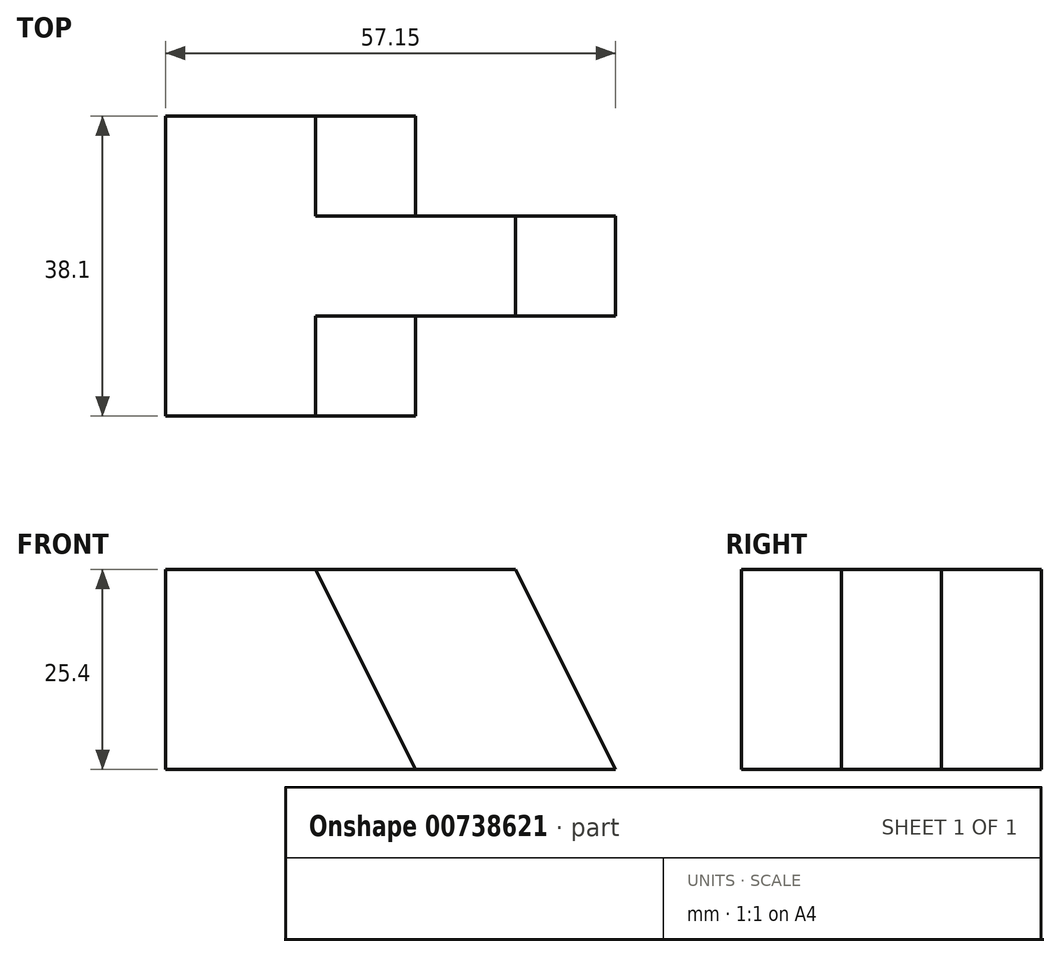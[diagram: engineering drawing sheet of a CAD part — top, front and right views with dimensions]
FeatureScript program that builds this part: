
annotation { "Feature Type Name" : "Feature", "Feature Type Description" : "" }
export const myFeature = defineFeature(function(context is Context, id is Id, definition is map)
    precondition{}
    {
        {
            var Q0;
            Q0=qCreatedBy(makeId("Front.planeOp"),FACE);
            var sketch = newSketch(context, id + "F0", { "sketchPlane" : qUnion([Q0])});
            skLineSegment(sketch, "E0.bottom", {"start": v(0, 0) * mm, "end": v(57.15, 0) * mm});
            skLineSegment(sketch, "E0.top", {"start": v(0, 25.4) * mm, "end": v(57.15, 25.4) * mm});
            skLineSegment(sketch, "E0.left", {"start": v(0, 0) * mm, "end": v(0, 25.4) * mm});
            skLineSegment(sketch, "E0.right", {"start": v(57.15, 0) * mm, "end": v(57.15, 25.4) * mm});
            skLineSegment(sketch, "E1", {"start": v(0, 25.4) * mm, "end": v(19.05, 25.4) * mm});
            skLineSegment(sketch, "E2", {"start": v(0, 0) * mm, "end": v(31.75, 0) * mm});
            skLineSegment(sketch, "E3", {"start": v(31.75, 0) * mm, "end": v(19.05, 25.4) * mm});
            skLineSegment(sketch, "E4", {"start": v(19.05, 25.4) * mm, "end": v(44.45, 25.4) * mm});
            skLineSegment(sketch, "E5", {"start": v(44.45, 25.4) * mm, "end": v(57.15, 0) * mm});
            skSolve(sketch);
        }
        {
            var Q0;
            {var subQ0=sQuery(id+"F0.wireOp",EDGE,"E0.left");Q0=makeQuery(id+"F0.imprint","IMPRINT",FACE,{"disambiguationData":[TD([[makeQuery(id+"F0.imprint","IMPRINT",EDGE,{"derivedFrom":subQ0}),-1.0]])]});}
            var Q1;
            {var subQ2=sQuery(id+"F0.wireOp",EDGE,"E3");Q1=makeQuery(id+"F0.imprint","IMPRINT",FACE,{"disambiguationData":[TD([[makeQuery(id+"F0.imprint","IMPRINT",EDGE,{"derivedFrom":subQ2}),-1.0]])]});}
            extrude(context, id + "F1", {"entities" : qUnion([Q0, Q1]), "oppositeDirection" : true, "depth" : 12.7 * mm, "offsetDistance" : 25.4 * mm});
        }
        {
            var Q0;
            Q0=makeQuery(id+"F1.opExtrude","CAP_FACE",FACE,{"disambiguationData":[OSD([sQuery(id+"F0.wireOp",EDGE,"E0.bottom"),sQuery(id+"F0.wireOp",EDGE,"E0.top"),sQuery(id+"F0.wireOp",EDGE,"E0.left"),sQuery(id+"F0.wireOp",EDGE,"E5")])],"isStart":true});
            var sketch = newSketch(context, id + "F2", { "sketchPlane" : qUnion([Q0])});
            skLineSegment(sketch, "E6", {"start": v(0, 25.4) * mm, "end": v(19.05, 25.4) * mm});
            skLineSegment(sketch, "E7", {"start": v(19.05, 25.4) * mm, "end": v(31.75, 0) * mm});
            skLineSegment(sketch, "E8", {"start": v(0, 0) * mm, "end": v(31.75, 0) * mm});
            skSolve(sketch);
        }
        {
            var Q0;
            Q0=makeQuery(id+"F2.imprint","IMPRINT",FACE,{"disambiguationData":[TD([[makeQuery(id+"F2.imprint","IMPRINT",EDGE,{"derivedFrom":sQuery(id+"F2.wireOp",EDGE,"E6")}),-1.0]])]});
            extrude(context, id + "F3", {"entities" : qUnion([Q0]), "operationType" : NewBodyOperationType.ADD, "oppositeDirection" : true, "depth" : 25.4 * mm, "offsetDistance" : 25.4 * mm});
        }
        {
            var Q0;
            Q0=makeQuery(id+"F3.opExtrude","CAP_FACE",FACE,{"disambiguationData":[OSD([sQuery(id+"F0.wireOp",EDGE,"E0.left"),sQuery(id+"F2.wireOp",EDGE,"E6"),sQuery(id+"F2.wireOp",EDGE,"E7"),sQuery(id+"F2.wireOp",EDGE,"E8")])],"isStart":false});
            extrude(context, id + "F4", {"entities" : qUnion([Q0]), "operationType" : NewBodyOperationType.ADD, "oppositeDirection" : true, "depth" : 38.1 * mm, "offsetDistance" : 25.4 * mm});
        }
    });
